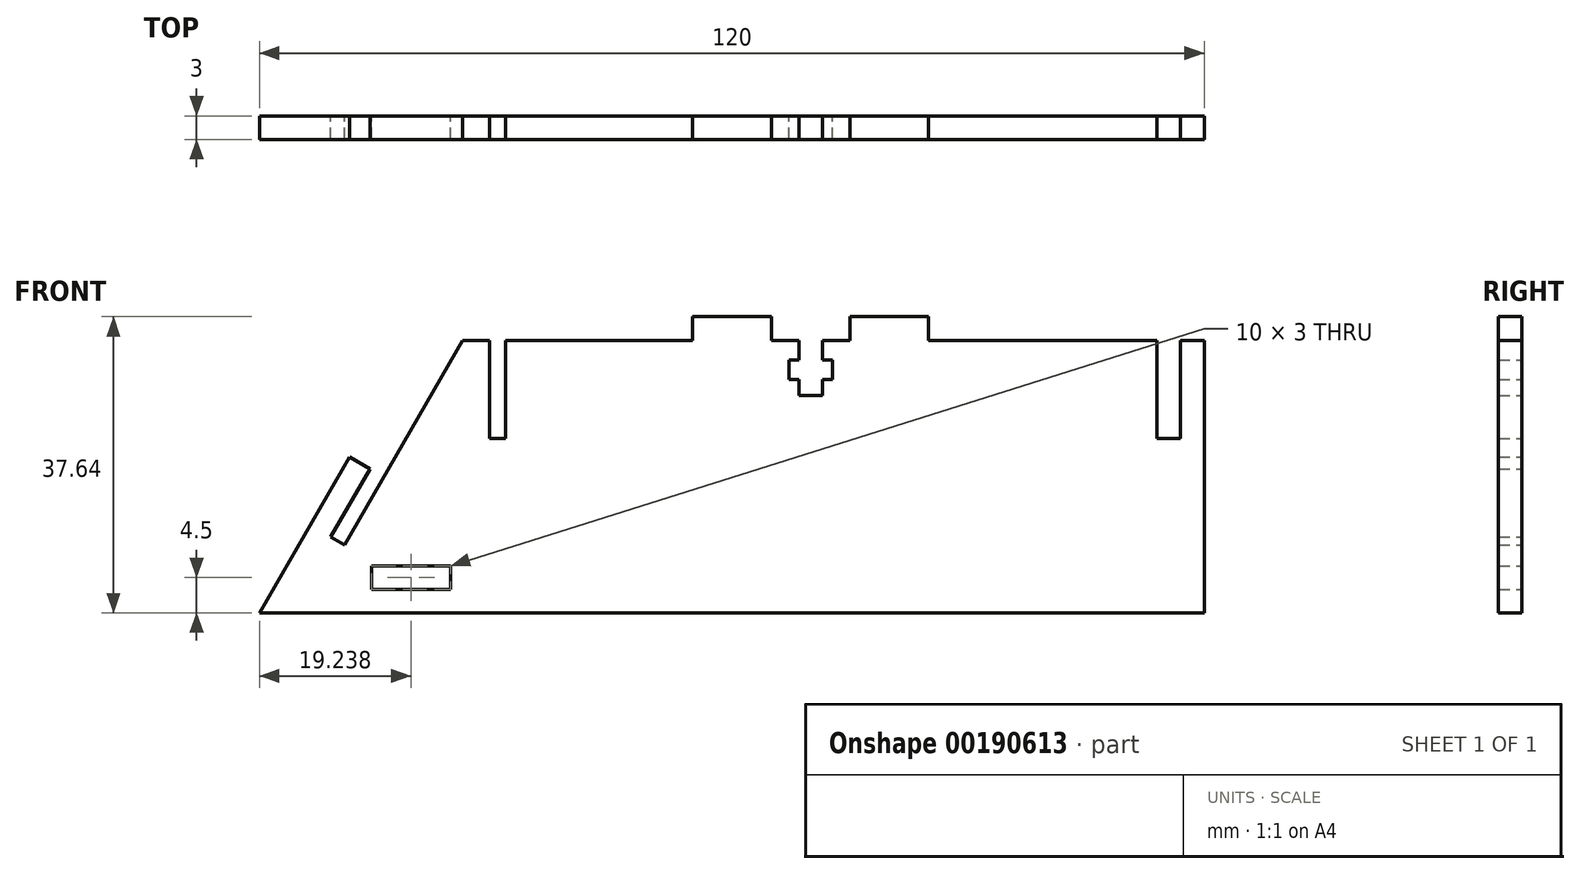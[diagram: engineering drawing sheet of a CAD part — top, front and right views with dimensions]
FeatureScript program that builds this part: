
annotation { "Feature Type Name" : "Feature", "Feature Type Description" : "" }
export const myFeature = defineFeature(function(context is Context, id is Id, definition is map)
    precondition{}
    {
        {
            var Q0;
            Q0=qCreatedBy(makeId("Front.planeOp"),FACE);
            var sketch = newSketch(context, id + "F0", { "sketchPlane" : qUnion([Q0])});
            skLineSegment(sketch, "E0", {"start": v(-94.23, 34.64) * mm, "end": v(-90.76, 34.64) * mm});
            skLineSegment(sketch, "E1", {"start": v(0, 34.64) * mm, "end": v(0, 0) * mm});
            skLineSegment(sketch, "E2", {"start": v(0, 0) * mm, "end": v(-120, 0) * mm});
            skLineSegment(sketch, "E3", {"start": v(-109.23, 8.66) * mm, "end": v(-110.96, 9.66) * mm});
            skLineSegment(sketch, "E4", {"start": v(-110.96, 9.66) * mm, "end": v(-105.96, 18.32) * mm});
            skLineSegment(sketch, "E5", {"start": v(-105.96, 18.32) * mm, "end": v(-108.56, 19.82) * mm});
            skLineSegment(sketch, "E6", {"start": v(-108.56, 19.82) * mm, "end": v(-120, 0) * mm});
            skLineSegment(sketch, "E7", {"start": v(-109.23, 8.66) * mm, "end": v(-94.23, 34.64) * mm});
            skLineSegment(sketch, "E8.bottom", {"start": v(-105.76, 3) * mm, "end": v(-95.76, 3) * mm});
            skLineSegment(sketch, "E8.top", {"start": v(-105.76, 6) * mm, "end": v(-95.76, 6) * mm});
            skLineSegment(sketch, "E8.left", {"start": v(-105.76, 3) * mm, "end": v(-105.76, 6) * mm});
            skLineSegment(sketch, "E8.right", {"start": v(-95.76, 3) * mm, "end": v(-95.76, 6) * mm});
            skLineSegment(sketch, "E9.top", {"start": v(-90.76, 22.14) * mm, "end": v(-88.76, 22.14) * mm});
            skLineSegment(sketch, "E9.left", {"start": v(-90.76, 34.64) * mm, "end": v(-90.76, 22.14) * mm});
            skLineSegment(sketch, "E9.right", {"start": v(-88.76, 34.64) * mm, "end": v(-88.76, 22.14) * mm});
            skLineSegment(sketch, "E10.top", {"start": v(-6, 22.14) * mm, "end": v(-3, 22.14) * mm});
            skLineSegment(sketch, "E10.left", {"start": v(-6, 34.64) * mm, "end": v(-6, 22.14) * mm});
            skLineSegment(sketch, "E10.right", {"start": v(-3, 34.64) * mm, "end": v(-3, 22.14) * mm});
            skLineSegment(sketch, "E11", {"start": v(-108.56, 19.82) * mm, "end": v(-100, 34.64) * mm, "construction": true});
            skLineSegment(sketch, "E12", {"start": v(-100, 34.64) * mm, "end": v(-94.23, 34.64) * mm, "construction": true});
            skLineSegment(sketch, "E13", {"start": v(-109.23, 8.66) * mm, "end": v(-114.23, 0) * mm, "construction": true});
            skPoint(sketch, "E14", {"position": v(-110.76, 6) * mm});
            skLineSegment(sketch, "E15.top", {"start": v(-65, 37.64) * mm, "end": v(-55, 37.64) * mm});
            skLineSegment(sketch, "E15.left", {"start": v(-65, 34.64) * mm, "end": v(-65, 37.64) * mm});
            skLineSegment(sketch, "E15.right", {"start": v(-55, 34.64) * mm, "end": v(-55, 37.64) * mm});
            skLineSegment(sketch, "E16", {"start": v(-55, 34.64) * mm, "end": v(-51.5, 34.64) * mm});
            skLineSegment(sketch, "E17", {"start": v(-45, 34.64) * mm, "end": v(-45, 37.64) * mm});
            skLineSegment(sketch, "E18", {"start": v(-45, 37.64) * mm, "end": v(-35, 37.64) * mm});
            skLineSegment(sketch, "E19", {"start": v(-35, 37.64) * mm, "end": v(-35, 34.64) * mm});
            skLineSegment(sketch, "E20", {"start": v(-35, 34.64) * mm, "end": v(-6, 34.64) * mm});
            skLineSegment(sketch, "E21", {"start": v(-51.5, 34.64) * mm, "end": v(-51.5, 32.14) * mm});
            skLineSegment(sketch, "E22", {"start": v(-51.5, 32.14) * mm, "end": v(-52.75, 32.14) * mm});
            skLineSegment(sketch, "E23", {"start": v(-52.75, 32.14) * mm, "end": v(-52.75, 29.64) * mm});
            skLineSegment(sketch, "E24", {"start": v(-52.75, 29.64) * mm, "end": v(-51.5, 29.64) * mm});
            skLineSegment(sketch, "E25", {"start": v(-51.5, 29.64) * mm, "end": v(-51.5, 27.64) * mm});
            skLineSegment(sketch, "E26", {"start": v(-51.5, 27.64) * mm, "end": v(-48.5, 27.64) * mm});
            skLineSegment(sketch, "E27", {"start": v(-48.5, 27.64) * mm, "end": v(-48.5, 29.64) * mm});
            skLineSegment(sketch, "E28", {"start": v(-48.5, 29.64) * mm, "end": v(-47.25, 29.64) * mm});
            skLineSegment(sketch, "E29", {"start": v(-47.25, 29.64) * mm, "end": v(-47.25, 32.14) * mm});
            skLineSegment(sketch, "E30", {"start": v(-47.25, 32.14) * mm, "end": v(-48.5, 32.14) * mm});
            skLineSegment(sketch, "E31", {"start": v(-48.5, 32.14) * mm, "end": v(-48.5, 34.64) * mm});
            skLineSegment(sketch, "E32", {"start": v(-48.5, 34.64) * mm, "end": v(-45, 34.64) * mm});
            skLineSegment(sketch, "E33", {"start": v(-3, 34.64) * mm, "end": v(0, 34.64) * mm});
            skLineSegment(sketch, "E34", {"start": v(-88.76, 34.64) * mm, "end": v(-65, 34.64) * mm});
            skSolve(sketch);
        }
        {
            var Q0;
            Q0=makeQuery(id+"F0.imprint","IMPRINT",FACE,{"disambiguationData":[TD([[makeQuery(id+"F0.imprint","IMPRINT",EDGE,{"derivedFrom":sQuery(id+"F0.wireOp",EDGE,"E0")}),-1.0]])]});
            extrude(context, id + "F1", {"entities" : qUnion([Q0]), "depth" : 3 * mm});
        }
    });
